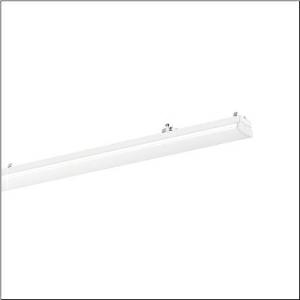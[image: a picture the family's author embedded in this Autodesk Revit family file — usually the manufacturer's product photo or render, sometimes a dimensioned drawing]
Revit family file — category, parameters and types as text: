
# Revit family: licross_r__11_recessed_opal_ho_51tl1dmn4d5m_ffb9
name_source: partatom
category: Lighting Fixtures
units: mm (PartAtom-declared; Revit-internal decimal feet)

## family parameters
Cut with Voids When Loaded = No
Host = Face
Light Source = No
Part Type = Normal
Room Calculation Point = No
Round Connector Dimension = Use Diameter
Shared = No

## types (1)
- --- (1 x LED, 13690 lm, 74.5 W, 4000K)
    Apparent Load = 75 VA
    CIE Flux Codes = 44 73 91 87 100
    Color Rendering = 80
    Color Temperature = 4000K
    Default Elevation = 1800 mm
    Description = Licross® 11 recessed opal HO, luminaire insert, of sheet steel, coil coated, white, length: 1.500mm, width: 76mm, height: 87mm, LED rated luminous flux: 13.690lm, light colour: 840, control gear: ON/OFF Multilumen, with plug, 3-pole, with phase selection, mains connection: 220..240V, AC, 50/60Hz, rated input power: 75W, halogen-free wiring, primary optical cover: cover, of PMMA, light emission: direct with ceiling illumination distribution, primary light characteristic: symmetric, protection rating (complete): IP40, insulation class (complete): insulation class I (protective earthing), certification: CE, ENEC, VDE, UKCA, protection symbol: D if used in an environment without relevant dust loads with corresponding accessories, impact resistance: IK06, permissible ambient temperature for indoor applications: -35..+35°C, corresponds to IFS (International Featured Standards) requirements for safety and quality in the food industry, reducing of maximum allowable ambient temperature of 5°C with ceiling mounting, packaging unit: 1 piece
    Height = 83 mm
    Lamp = 1 x LED
    Lamp Light Flux = 13690 lm
    Lamp Power = 74.5 W
    Lamp count = 1
    Length = 1500 mm
    Luminous efficacy = 184 lm/W
    Manufacturer = Siteco
    ModVariant = No
    Model = 51TL1DMN4D5M
    Mounting Place = Ceiling
    Mounting Type = Pendant
    Number of Poles = 1
    OnlyDefault = Yes
    Power Factor = 1
    Product Name = Licross® 11 recessed opal HO
    Product group = luminaire insert
    ProductGroupID = 902
    Protection Class = Protection class I
    Protection Degree = IP 40
    RLX_Detail_Level = 1
    RLX_Emergency_Light_Flux = 0 lm
    RLX_Emergency_Type = 0
    RLX_Emergency_Type_DB = No
    RlxData = <blob elided: 24805 chars, md5=450f6fa8>
    Socket = socket
    Standby Power = 0 W
    System Light Flux = 13690 lm
    System Power = 75 W
    Type Comments = factory setting: luminous flux: 100 % | (A | C | E) | 174 mA
    Type Image = l_1313666.jpg
    URL = http://relux.com
    VarID = @adj_075810
    Voltage = 0 V
    Weight = 0.00 kg
    Width = 76 mm

## geometry (parser evidence)
native form markers: Blend x4, Sweep x12
no freeform markers — native parametric forms only
